# Revit family: Deca_Ducha higiênica com registro e derivação_Izy Plus_1984.24.ACT
name_source: partatom
category: Plumbing Fixtures
units: mm (PartAtom-declared; Revit-internal decimal feet)

## family parameters
Cut with Voids When Loaded = No
Host = Face
Part Type = Normal
Room Calculation Point = No
Round Connector Dimension = Use Radius
Shared = No

## types (2) — shared parameters
Aprovado por = quattroD
Atendimento ao Cliente = 0800-0117073
Categoria = Metais para banheiro
Composição Básica = Liga cobre (bronze e latão);Aço;Plástico de Engenharia;Elastômeros
Consumo = Otimização do jato de água
Cor Principal = Cromado
Criado por = quattroD
Código Pai = 1984.24.ACT
Default Elevation = 0.7 m
Diâmetro Água Fria = 0.02 m
Diâmetro Água Fria Saída = 0.02 m
Linha = Izy Plus
Manufacturer = DECA
Material = Deca_Cromado
Norma = NBR14877
Peso Líquido (Kg) = 0.684
Pressão máx. funcionamento = 40
Pressão mín. funcionamento = 2
Raio Água Fria = 0.01 m
Raio Água Fria Saída = 0.01 m
Segmento = Banheiro Médio (D42)
Tipo de dispositivo economizador = Sim
Tipo de mecanismo utilizado = MVC -1/4 volta
Tipo de rosca de entrada = BSP NBR 8133
URL = www.deca.com.br
Vazão na Pressão máx. (L/min) = 6
Vazão na Pressão mín. (L/min) = 4

## per-type parameters (varying)
| type | Cor Secundária | Material Secundário | Model |
| 1984.C24.ACT.CR_Cromado |  | Deca_Cromado | 1984.C24.ACT.CR |
| 1984.C24.ACT.BR_Branco | Branco | Deca_Branco | 1984.C24.ACT.BR |

## geometry (parser evidence)
native form markers: Sweep x2
no freeform markers — native parametric forms only
